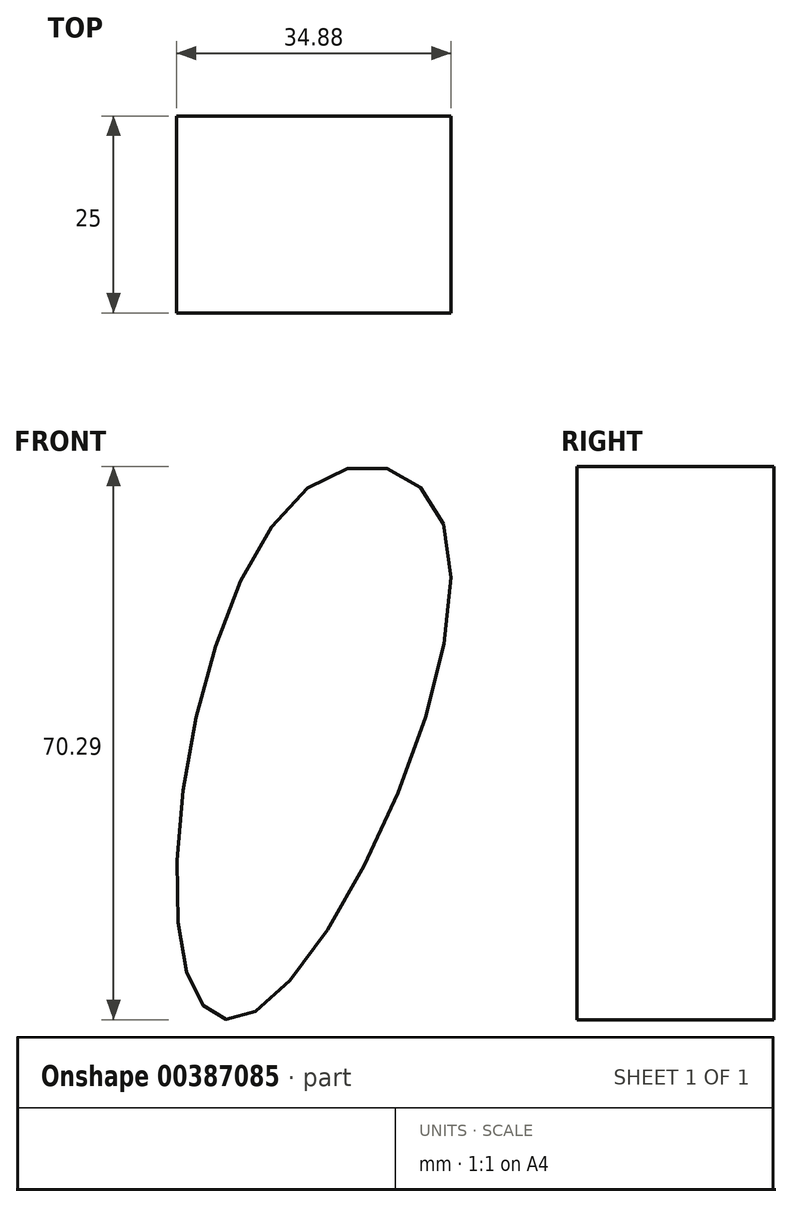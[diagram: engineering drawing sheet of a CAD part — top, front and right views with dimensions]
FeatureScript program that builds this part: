
annotation { "Feature Type Name" : "Feature", "Feature Type Description" : "" }
export const myFeature = defineFeature(function(context is Context, id is Id, definition is map)
    precondition{}
    {
        {
            var Q0;
            Q0=qCreatedBy(makeId("Front.planeOp"),FACE);
            var sketch = newSketch(context, id + "F0", { "sketchPlane" : qUnion([Q0])});
            skFitSpline(sketch, "E0", {"points": [v(-45.52, 0) * mm, v(-61.41, -59.28) * mm, v(-52.36, -66.62) * mm, v(-27.93, -5.64) * mm, v(-45.52, 0) * mm]});
            skSolve(sketch);
        }
        {
            var Q0;
            Q0=makeQuery(id+"F0.imprint","IMPRINT",FACE,{"disambiguationData":[TD([[makeQuery(id+"F0.imprint","IMPRINT",EDGE,{"derivedFrom":sQuery(id+"F0.wireOp",EDGE,"E0")}),1.0]])]});
            extrude(context, id + "F1", {"entities" : qUnion([Q0]), "depth" : 25 * mm});
        }
    });
